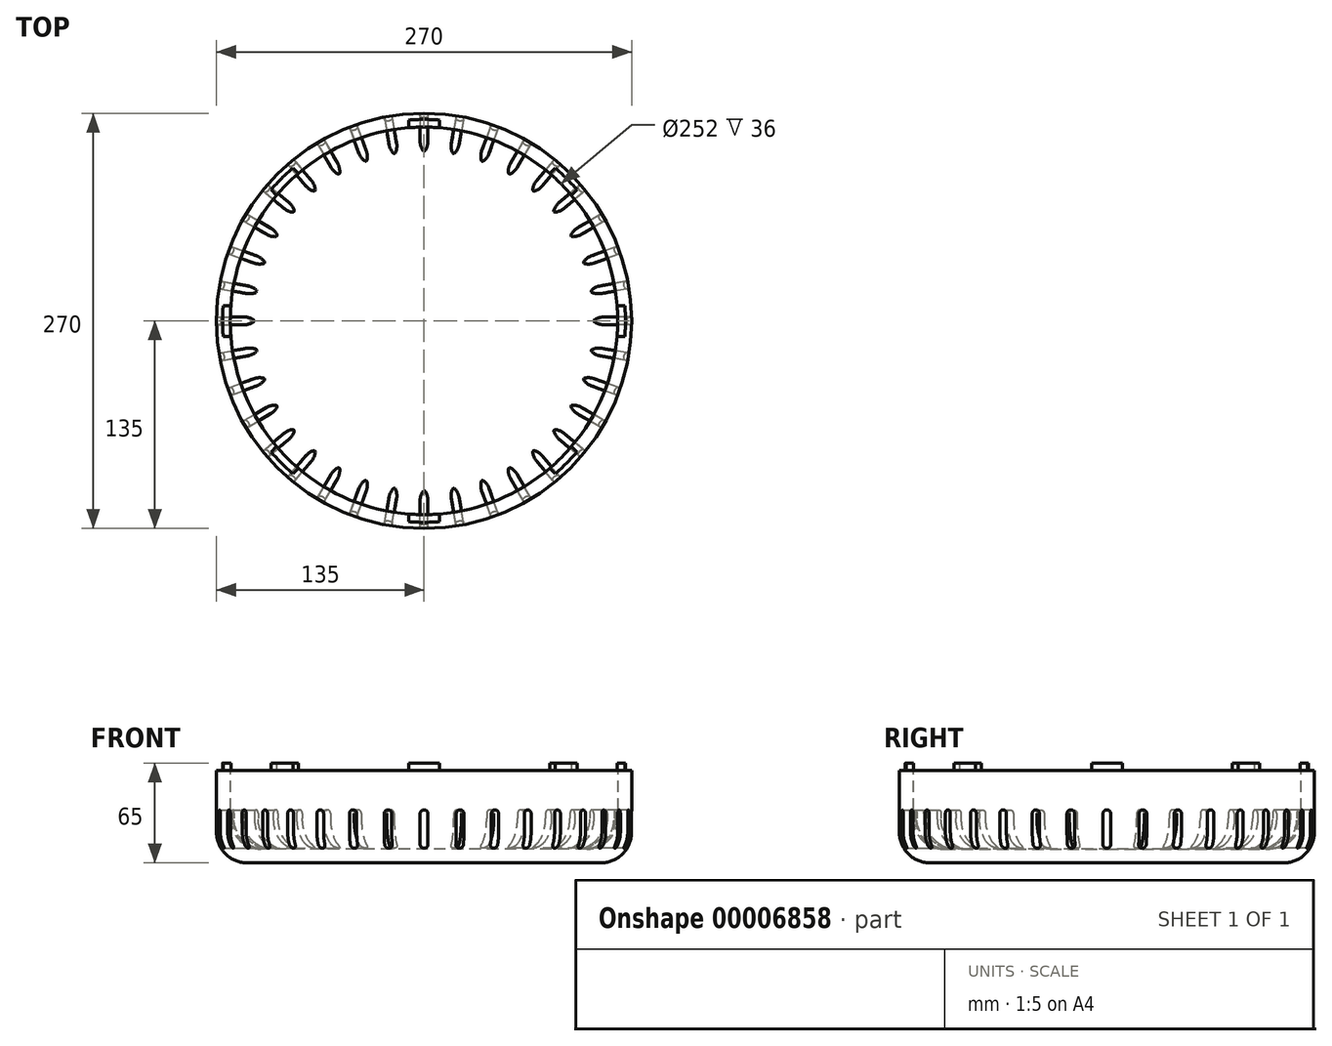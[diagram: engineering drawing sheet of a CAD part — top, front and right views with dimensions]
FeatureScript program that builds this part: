
annotation { "Feature Type Name" : "Feature", "Feature Type Description" : "" }
export const myFeature = defineFeature(function(context is Context, id is Id, definition is map)
    precondition{}
    {
        {
            var Q0;
            Q0=qCreatedBy(makeId("Top.planeOp"),FACE);
            var sketch = newSketch(context, id + "F0", { "sketchPlane" : qUnion([Q0])});
            skCircle(sketch, "E0", {"center": v(0, 0) * mm, "radius": 126 * mm});
            skCircle(sketch, "E1", {"center": v(0, 0) * mm, "radius": 135 * mm});
            skSolve(sketch);
        }
        {
            var Q0;
            Q0=qSketchRegion(id+"F0",true);
            var Q1;
            Q1=makeQuery(id+"F0.imprint","IMPRINT",FACE,{"disambiguationData":[TD([[makeQuery(id+"F0.imprint","IMPRINT",EDGE,{"derivedFrom":sQuery(id+"F0.wireOp",EDGE,"ITGFbY2j-F6Gs-mvNy-kfQ0-MyUqCA95ELIB")}),-1.0]])]});
            var Q2;
            Q2=makeQuery(id+"F0.imprint","IMPRINT",FACE,{"disambiguationData":[TD([[makeQuery(id+"F0.imprint","IMPRINT",EDGE,{"derivedFrom":sQuery(id+"F0.wireOp",EDGE,"ITGFbY2j-F6Gs-mvNy-kfQ0-MyUqCA95ELIB")}),1.0]])]});
            var Q3;
            Q3=makeQuery(id+"F0.imprint","IMPRINT",FACE,{"disambiguationData":[TD([[makeQuery(id+"F0.imprint","IMPRINT",EDGE,{"derivedFrom":sQuery(id+"F0.wireOp",EDGE,"E0")}),1.0]])]});
            extrude(context, id + "F1", {"entities" : qUnion([Q0, Q1, Q2, Q3]), "oppositeDirection" : true, "depth" : 30 * mm});
        }
        {
            var Q0;
            Q0=makeQuery(id+"F0.imprint","IMPRINT",FACE,{"disambiguationData":[TD([[makeQuery(id+"F0.imprint","IMPRINT",EDGE,{"derivedFrom":sQuery(id+"F0.wireOp",EDGE,"E0")}),-1.0]])]});
            extrude(context, id + "F2", {"entities" : qUnion([Q0]), "operationType" : NewBodyOperationType.ADD, "depth" : 30 * mm});
        }
        {
            var Q0;
            Q0=makeQuery(id+"F1.opExtrude","CAP_FACE",FACE,{"disambiguationData":[OSD([sQuery(id+"F0.wireOp",EDGE,"E1")])],"isStart":true});
            shell(context, id + "F3", {"entities" : qUnion([Q0]), "thickness" : 9 * mm});
        }
        {
            var Q0;
            Q0=makeQuery(id+"F2.opExtrude","CAP_FACE",FACE,{"disambiguationData":[OSD([sQuery(id+"F0.wireOp",EDGE,"E0"),sQuery(id+"F0.wireOp",EDGE,"E1")])],"isStart":false});
            var sketch = newSketch(context, id + "F4", { "sketchPlane" : qUnion([Q0])});
            skCircle(sketch, "E2", {"center": v(0, 0) * mm, "radius": 126 * mm});
            skCircle(sketch, "E3", {"center": v(0, 0) * mm, "radius": 131 * mm});
            skLineSegment(sketch, "E4", {"start": v(-130.62, -10) * mm, "end": v(-125.6, -10) * mm});
            skLineSegment(sketch, "E5", {"start": v(-130.62, 10) * mm, "end": v(-125.6, 10) * mm});
            skLineSegment(sketch, "E6", {"start": v(125.6, 10) * mm, "end": v(130.62, 10) * mm});
            skLineSegment(sketch, "E7", {"start": v(125.6, -10) * mm, "end": v(130.62, -10) * mm});
            skLineSegment(sketch, "E8", {"start": v(-10, 125.6) * mm, "end": v(-10, 130.62) * mm});
            skLineSegment(sketch, "E9", {"start": v(10, 125.6) * mm, "end": v(10, 130.62) * mm});
            skPoint(sketch, "E10", {"position": v(0, 126) * mm});
            skPoint(sketch, "E11", {"position": v(-126, 0) * mm});
            skPoint(sketch, "E12", {"position": v(126, 0) * mm});
            skPoint(sketch, "E13", {"position": v(0, -126) * mm});
            skLineSegment(sketch, "E14", {"start": v(-128.11, 10) * mm, "end": v(-128.11, -10) * mm});
            skPoint(sketch, "E15", {"position": v(-128.11, 0) * mm});
            skLineSegment(sketch, "E16", {"start": v(164.04, 10) * mm, "end": v(164.04, -10) * mm});
            skPoint(sketch, "E17", {"position": v(164.04, 0) * mm});
            skLineSegment(sketch, "E18", {"start": v(-10, -125.6) * mm, "end": v(-10, -130.62) * mm});
            skLineSegment(sketch, "E19", {"start": v(10, -125.6) * mm, "end": v(10, -130.62) * mm});
            skLineSegment(sketch, "E20", {"start": v(-10, -126.16) * mm, "end": v(10, -126.16) * mm});
            skPoint(sketch, "E21", {"position": v(0, -126.16) * mm});
            skLineSegment(sketch, "E22", {"start": v(-10, 175.22) * mm, "end": v(10, 175.22) * mm});
            skPoint(sketch, "E23", {"position": v(0, 175.22) * mm});
            skLineSegment(sketch, "E24", {"start": v(0, 0) * mm, "end": v(0, 71.25) * mm});
            skLineSegment(sketch, "E25", {"start": v(23.85, 0) * mm, "end": v(0, 0) * mm});
            skLineSegment(sketch, "E26", {"start": v(-90.59, 90.59) * mm, "end": v(90.59, -90.59) * mm});
            skLineSegment(sketch, "E27", {"start": v(-43.26, -43.26) * mm, "end": v(90.59, 90.59) * mm});
            skLineSegment(sketch, "E28", {"start": v(81.74, 95.89) * mm, "end": v(85.29, 99.43) * mm});
            skLineSegment(sketch, "E29", {"start": v(95.89, 81.74) * mm, "end": v(99.43, 85.29) * mm});
            skLineSegment(sketch, "E30", {"start": v(83.52, 97.66) * mm, "end": v(97.66, 83.52) * mm});
            skPoint(sketch, "E31", {"position": v(90.59, 90.59) * mm});
            skLineSegment(sketch, "E32", {"start": v(-99.43, -85.29) * mm, "end": v(-95.89, -81.74) * mm});
            skLineSegment(sketch, "E33", {"start": v(-85.29, -99.43) * mm, "end": v(-81.74, -95.89) * mm});
            skLineSegment(sketch, "E34", {"start": v(-50.33, -36.19) * mm, "end": v(-36.19, -50.33) * mm});
            skPoint(sketch, "E35", {"position": v(-43.26, -43.26) * mm});
            skLineSegment(sketch, "E36", {"start": v(95.89, -81.74) * mm, "end": v(99.43, -85.29) * mm});
            skLineSegment(sketch, "E37", {"start": v(81.74, -95.89) * mm, "end": v(85.29, -99.43) * mm});
            skLineSegment(sketch, "E38", {"start": v(83.52, -97.66) * mm, "end": v(97.66, -83.52) * mm});
            skPoint(sketch, "E39", {"position": v(90.59, -90.59) * mm});
            skLineSegment(sketch, "E40", {"start": v(-85.29, 99.43) * mm, "end": v(-81.74, 95.89) * mm});
            skLineSegment(sketch, "E41", {"start": v(-99.43, 85.29) * mm, "end": v(-95.89, 81.74) * mm});
            skLineSegment(sketch, "E42", {"start": v(-97.66, 83.52) * mm, "end": v(-83.52, 97.66) * mm});
            skPoint(sketch, "E43", {"position": v(-90.59, 90.59) * mm});
            skSolve(sketch);
        }
        {
            var Q0;
            {var subQ5=sQuery(id+"F4.wireOp",EDGE,"E14");Q0=makeQuery(id+"F4.imprint","IMPRINT",FACE,{"disambiguationData":[TD([[makeQuery(id+"F4.imprint","IMPRINT",EDGE,{"derivedFrom":subQ5}),-1.0]])]});}
            var Q1;
            {var subQ5=sQuery(id+"F4.wireOp",EDGE,"E14");Q1=makeQuery(id+"F4.imprint","IMPRINT",FACE,{"disambiguationData":[TD([[makeQuery(id+"F4.imprint","IMPRINT",EDGE,{"derivedFrom":subQ5}),1.0]])]});}
            var Q2;
            {var subQ5=sQuery(id+"F4.wireOp",EDGE,"E22");Q2=makeQuery(id+"F4.imprint","IMPRINT",FACE,{"disambiguationData":[TD([[makeQuery(id+"F4.imprint","IMPRINT",EDGE,{"derivedFrom":subQ5}),-1.0]])]});}
            var Q3;
            {var subQ5=sQuery(id+"F4.wireOp",EDGE,"E22");Q3=makeQuery(id+"F4.imprint","IMPRINT",FACE,{"disambiguationData":[TD([[makeQuery(id+"F4.imprint","IMPRINT",EDGE,{"derivedFrom":subQ5}),1.0]])]});}
            var Q4;
            {var subQ5=sQuery(id+"F4.wireOp",EDGE,"E16");Q4=makeQuery(id+"F4.imprint","IMPRINT",FACE,{"disambiguationData":[TD([[makeQuery(id+"F4.imprint","IMPRINT",EDGE,{"derivedFrom":subQ5}),1.0]])]});}
            var Q5;
            {var subQ5=sQuery(id+"F4.wireOp",EDGE,"E20");Q5=makeQuery(id+"F4.imprint","IMPRINT",FACE,{"disambiguationData":[TD([[makeQuery(id+"F4.imprint","IMPRINT",EDGE,{"derivedFrom":subQ5}),-1.0]])]});}
            var Q6;
            {var subQ5=sQuery(id+"F4.wireOp",EDGE,"E20");Q6=makeQuery(id+"F4.imprint","IMPRINT",FACE,{"disambiguationData":[TD([[makeQuery(id+"F4.imprint","IMPRINT",EDGE,{"derivedFrom":subQ5}),1.0]])]});}
            var Q7;
            {var subQ5=sQuery(id+"F4.wireOp",EDGE,"E16");Q7=makeQuery(id+"F4.imprint","IMPRINT",FACE,{"disambiguationData":[TD([[makeQuery(id+"F4.imprint","IMPRINT",EDGE,{"derivedFrom":subQ5}),-1.0]])]});}
            var Q8;
            {var subQ0=sQuery(id+"F4.wireOp",EDGE,"E6");Q8=makeQuery(id+"F4.imprint","IMPRINT",FACE,{"disambiguationData":[TD([[makeQuery(id+"F4.imprint","IMPRINT",EDGE,{"derivedFrom":subQ0}),-1.0]])]});}
            var Q9;
            {var subQ0=sQuery(id+"F4.wireOp",EDGE,"E8");Q9=makeQuery(id+"F4.imprint","IMPRINT",FACE,{"disambiguationData":[TD([[makeQuery(id+"F4.imprint","IMPRINT",EDGE,{"derivedFrom":subQ0}),-1.0]])]});}
            extrude(context, id + "F5", {"entities" : qUnion([Q0, Q1, Q2, Q3, Q4, Q5, Q6, Q7, Q8, Q9]), "operationType" : NewBodyOperationType.ADD, "depth" : 5 * mm});
        }
        {
            var Q0;
            {var subQ4=sQuery(id+"F4.wireOp",EDGE,"E3");var subQ6=sQuery(id+"F4.wireOp",EDGE,"E40");var subQ7=makeQuery(id+"F4.imprint","INTERSECT",VERTEX,{"derivedFrom":[subQ4,subQ6]});Q0=makeQuery(id+"F4.imprint","IMPRINT",FACE,{"disambiguationData":[TD([[makeQuery(id+"F4.imprint","IMPRINT",EDGE,{"disambiguationData":[TD([[subQ7,-1.0]])],"derivedFrom":subQ4}),1.0]])]});}
            var Q1;
            {var subQ0=sQuery(id+"F4.wireOp",EDGE,"E41");var subQ1=sQuery(id+"F4.wireOp",EDGE,"E2");var subQ2=makeQuery(id+"F4.imprint","INTERSECT",VERTEX,{"derivedFrom":[subQ1,subQ0]});Q1=makeQuery(id+"F4.imprint","IMPRINT",FACE,{"disambiguationData":[TD([[makeQuery(id+"F4.imprint","IMPRINT",EDGE,{"disambiguationData":[TD([[subQ2,1.0]])],"derivedFrom":subQ1}),-1.0]])]});}
            var Q2;
            {var subQ0=sQuery(id+"F4.wireOp",EDGE,"E40");var subQ1=sQuery(id+"F4.wireOp",EDGE,"E2");var subQ2=makeQuery(id+"F4.imprint","INTERSECT",VERTEX,{"derivedFrom":[subQ1,subQ0]});Q2=makeQuery(id+"F4.imprint","IMPRINT",FACE,{"disambiguationData":[TD([[makeQuery(id+"F4.imprint","IMPRINT",EDGE,{"disambiguationData":[TD([[subQ2,-1.0]])],"derivedFrom":subQ1}),-1.0]])]});}
            var Q3;
            {var subQ2=sQuery(id+"F4.wireOp",EDGE,"E28");var subQ5=sQuery(id+"F4.wireOp",EDGE,"E3");var subQ8=makeQuery(id+"F4.imprint","INTERSECT",VERTEX,{"derivedFrom":[subQ5,subQ2]});Q3=makeQuery(id+"F4.imprint","IMPRINT",FACE,{"disambiguationData":[TD([[makeQuery(id+"F4.imprint","IMPRINT",EDGE,{"disambiguationData":[TD([[subQ8,1.0]])],"derivedFrom":subQ5}),1.0]])]});}
            var Q4;
            {var subQ0=sQuery(id+"F4.wireOp",EDGE,"E28");var subQ1=sQuery(id+"F4.wireOp",EDGE,"E2");var subQ2=makeQuery(id+"F4.imprint","INTERSECT",VERTEX,{"derivedFrom":[subQ1,subQ0]});Q4=makeQuery(id+"F4.imprint","IMPRINT",FACE,{"disambiguationData":[TD([[makeQuery(id+"F4.imprint","IMPRINT",EDGE,{"disambiguationData":[TD([[subQ2,1.0]])],"derivedFrom":subQ1}),-1.0]])]});}
            var Q5;
            {var subQ0=sQuery(id+"F4.wireOp",EDGE,"E29");var subQ1=sQuery(id+"F4.wireOp",EDGE,"E2");var subQ2=makeQuery(id+"F4.imprint","INTERSECT",VERTEX,{"derivedFrom":[subQ1,subQ0]});Q5=makeQuery(id+"F4.imprint","IMPRINT",FACE,{"disambiguationData":[TD([[makeQuery(id+"F4.imprint","IMPRINT",EDGE,{"disambiguationData":[TD([[subQ2,-1.0]])],"derivedFrom":subQ1}),-1.0]])]});}
            var Q6;
            {var subQ0=sQuery(id+"F4.wireOp",EDGE,"E36");var subQ1=sQuery(id+"F4.wireOp",EDGE,"E2");var subQ2=makeQuery(id+"F4.imprint","INTERSECT",VERTEX,{"derivedFrom":[subQ1,subQ0]});Q6=makeQuery(id+"F4.imprint","IMPRINT",FACE,{"disambiguationData":[TD([[makeQuery(id+"F4.imprint","IMPRINT",EDGE,{"disambiguationData":[TD([[subQ2,1.0]])],"derivedFrom":subQ1}),-1.0]])]});}
            var Q7;
            {var subQ0=sQuery(id+"F4.wireOp",EDGE,"E37");var subQ1=sQuery(id+"F4.wireOp",EDGE,"E2");var subQ2=makeQuery(id+"F4.imprint","INTERSECT",VERTEX,{"derivedFrom":[subQ1,subQ0]});Q7=makeQuery(id+"F4.imprint","IMPRINT",FACE,{"disambiguationData":[TD([[makeQuery(id+"F4.imprint","IMPRINT",EDGE,{"disambiguationData":[TD([[subQ2,-1.0]])],"derivedFrom":subQ1}),-1.0]])]});}
            var Q8;
            {var subQ1=sQuery(id+"F4.wireOp",EDGE,"E3");var subQ6=sQuery(id+"F4.wireOp",EDGE,"E36");var subQ7=makeQuery(id+"F4.imprint","INTERSECT",VERTEX,{"derivedFrom":[subQ1,subQ6]});Q8=makeQuery(id+"F4.imprint","IMPRINT",FACE,{"disambiguationData":[TD([[makeQuery(id+"F4.imprint","IMPRINT",EDGE,{"disambiguationData":[TD([[subQ7,1.0]])],"derivedFrom":subQ1}),1.0]])]});}
            var Q9;
            {var subQ0=sQuery(id+"F4.wireOp",EDGE,"E33");var subQ1=sQuery(id+"F4.wireOp",EDGE,"E2");var subQ2=makeQuery(id+"F4.imprint","INTERSECT",VERTEX,{"derivedFrom":[subQ1,subQ0]});Q9=makeQuery(id+"F4.imprint","IMPRINT",FACE,{"disambiguationData":[TD([[makeQuery(id+"F4.imprint","IMPRINT",EDGE,{"disambiguationData":[TD([[subQ2,1.0]])],"derivedFrom":subQ1}),-1.0]])]});}
            var Q10;
            {var subQ0=sQuery(id+"F4.wireOp",EDGE,"E32");var subQ1=sQuery(id+"F4.wireOp",EDGE,"E2");var subQ2=makeQuery(id+"F4.imprint","INTERSECT",VERTEX,{"derivedFrom":[subQ1,subQ0]});Q10=makeQuery(id+"F4.imprint","IMPRINT",FACE,{"disambiguationData":[TD([[makeQuery(id+"F4.imprint","IMPRINT",EDGE,{"disambiguationData":[TD([[subQ2,-1.0]])],"derivedFrom":subQ1}),-1.0]])]});}
            var Q11;
            {var subQ1=sQuery(id+"F4.wireOp",EDGE,"E3");var subQ5=sQuery(id+"F4.wireOp",EDGE,"E32");var subQ6=makeQuery(id+"F4.imprint","INTERSECT",VERTEX,{"derivedFrom":[subQ1,subQ5]});Q11=makeQuery(id+"F4.imprint","IMPRINT",FACE,{"disambiguationData":[TD([[makeQuery(id+"F4.imprint","IMPRINT",EDGE,{"disambiguationData":[TD([[subQ6,-1.0]])],"derivedFrom":subQ1}),1.0]])]});}
            extrude(context, id + "F6", {"entities" : qUnion([Q0, Q1, Q2, Q3, Q4, Q5, Q6, Q7, Q8, Q9, Q10, Q11]), "operationType" : NewBodyOperationType.ADD, "depth" : 5 * mm});
        }
        {
            var Q0;
            Q0=qCreatedBy(makeId("Front.planeOp"),FACE);
            cPlane(context, id + "F7", {"entities" : qUnion([Q0]), "cplaneType" : CPlaneType.OFFSET, "offset" : 120 * mm, "width" : 150 * mm, "height" : 150 * mm});
        }
        {
            var Q0;
            Q0=qCreatedBy(id+"F7.planeOp",FACE);
            var sketch = newSketch(context, id + "F8", { "sketchPlane" : qUnion([Q0])});
            skLineSegment(sketch, "E44.bottom", {"start": v(-2.5, -18) * mm, "end": v(2.5, -18) * mm});
            skLineSegment(sketch, "E44.top", {"start": v(-2.5, 2) * mm, "end": v(2.5, 2) * mm});
            skLineSegment(sketch, "E44.left", {"start": v(-2.5, -18) * mm, "end": v(-2.5, 2) * mm});
            skLineSegment(sketch, "E44.right", {"start": v(2.5, -18) * mm, "end": v(2.5, 2) * mm});
            skPoint(sketch, "E45", {"position": v(0, 2) * mm});
            skPoint(sketch, "E45.positionSnap0", {"position": v(0, 2) * mm});
            skPoint(sketch, "E46", {"position": v(0, 0) * mm});
            skArc(sketch, "E47", {"start": v(2.5, 2) * mm, "mid": v(0, 4.5) * mm, "end": v(-2.5, 2) * mm});
            skArc(sketch, "E48", {"start": v(-2.5, -18) * mm, "mid": v(0, -20.5) * mm, "end": v(2.5, -18) * mm});
            skSolve(sketch);
        }
        {
            var Q0;
            Q0=qSketchRegion(id+"F8",true);
            extrude(context, id + "F9", {"entities" : qUnion([Q0]), "depth" : 25 * mm});
        }
        {
            var Q0;
            Q0=makeQuery(id+"F9.opExtrude","SWEPT_BODY",BODY,{"disambiguationData":[OSD([sQuery(id+"F8.wireOp",EDGE,"E44.bottom"),sQuery(id+"F8.wireOp",EDGE,"E44.top"),sQuery(id+"F8.wireOp",EDGE,"E44.left"),sQuery(id+"F8.wireOp",EDGE,"E44.right")])]});
            var Q1;
            Q1=makeQuery(id+"F2.opExtrude","CAP_EDGE",EDGE,{"disambiguationData":[OSD([sQuery(id+"F0.wireOp",EDGE,"E1")])],"isStart":false});
            circularPattern(context, id + "F10", {"entities" : qUnion([Q0]), "axis" : qUnion([Q1]), "angle" : 10 * degree, "instanceCount" : 40});
        }
        {
            var Q0;
            Q0=makeQuery(id+"F9.opExtrude","SWEPT_BODY",BODY,{"disambiguationData":[OSD([sQuery(id+"F8.wireOp",EDGE,"E44.bottom"),sQuery(id+"F8.wireOp",EDGE,"E44.top"),sQuery(id+"F8.wireOp",EDGE,"E44.left"),sQuery(id+"F8.wireOp",EDGE,"E44.right")])]});
            var Q1;
            Q1=makeQuery(id+"F10.opPattern","COPY",BODY,{"derivedFrom":makeQuery(id+"F9.opExtrude","SWEPT_BODY",BODY,{"disambiguationData":[OSD([sQuery(id+"F8.wireOp",EDGE,"E44.bottom"),sQuery(id+"F8.wireOp",EDGE,"E44.top"),sQuery(id+"F8.wireOp",EDGE,"E44.left"),sQuery(id+"F8.wireOp",EDGE,"E44.right")])]}),"instanceName":"1"});
            var Q2;
            Q2=makeQuery(id+"F10.opPattern","COPY",BODY,{"derivedFrom":makeQuery(id+"F9.opExtrude","SWEPT_BODY",BODY,{"disambiguationData":[OSD([sQuery(id+"F8.wireOp",EDGE,"E44.bottom"),sQuery(id+"F8.wireOp",EDGE,"E44.top"),sQuery(id+"F8.wireOp",EDGE,"E44.left"),sQuery(id+"F8.wireOp",EDGE,"E44.right")])]}),"instanceName":"2"});
            var Q3;
            Q3=makeQuery(id+"F10.opPattern","COPY",BODY,{"derivedFrom":makeQuery(id+"F9.opExtrude","SWEPT_BODY",BODY,{"disambiguationData":[OSD([sQuery(id+"F8.wireOp",EDGE,"E44.bottom"),sQuery(id+"F8.wireOp",EDGE,"E44.top"),sQuery(id+"F8.wireOp",EDGE,"E44.left"),sQuery(id+"F8.wireOp",EDGE,"E44.right")])]}),"instanceName":"3"});
            var Q4;
            Q4=makeQuery(id+"F10.opPattern","COPY",BODY,{"derivedFrom":makeQuery(id+"F9.opExtrude","SWEPT_BODY",BODY,{"disambiguationData":[OSD([sQuery(id+"F8.wireOp",EDGE,"E44.bottom"),sQuery(id+"F8.wireOp",EDGE,"E44.top"),sQuery(id+"F8.wireOp",EDGE,"E44.left"),sQuery(id+"F8.wireOp",EDGE,"E44.right")])]}),"instanceName":"4"});
            var Q5;
            Q5=makeQuery(id+"F10.opPattern","COPY",BODY,{"derivedFrom":makeQuery(id+"F9.opExtrude","SWEPT_BODY",BODY,{"disambiguationData":[OSD([sQuery(id+"F8.wireOp",EDGE,"E44.bottom"),sQuery(id+"F8.wireOp",EDGE,"E44.top"),sQuery(id+"F8.wireOp",EDGE,"E44.left"),sQuery(id+"F8.wireOp",EDGE,"E44.right")])]}),"instanceName":"5"});
            var Q6;
            Q6=makeQuery(id+"F10.opPattern","COPY",BODY,{"derivedFrom":makeQuery(id+"F9.opExtrude","SWEPT_BODY",BODY,{"disambiguationData":[OSD([sQuery(id+"F8.wireOp",EDGE,"E44.bottom"),sQuery(id+"F8.wireOp",EDGE,"E44.top"),sQuery(id+"F8.wireOp",EDGE,"E44.left"),sQuery(id+"F8.wireOp",EDGE,"E44.right")])]}),"instanceName":"6"});
            var Q7;
            Q7=makeQuery(id+"F10.opPattern","COPY",BODY,{"derivedFrom":makeQuery(id+"F9.opExtrude","SWEPT_BODY",BODY,{"disambiguationData":[OSD([sQuery(id+"F8.wireOp",EDGE,"E44.bottom"),sQuery(id+"F8.wireOp",EDGE,"E44.top"),sQuery(id+"F8.wireOp",EDGE,"E44.left"),sQuery(id+"F8.wireOp",EDGE,"E44.right")])]}),"instanceName":"7"});
            var Q8;
            Q8=makeQuery(id+"F10.opPattern","COPY",BODY,{"derivedFrom":makeQuery(id+"F9.opExtrude","SWEPT_BODY",BODY,{"disambiguationData":[OSD([sQuery(id+"F8.wireOp",EDGE,"E44.bottom"),sQuery(id+"F8.wireOp",EDGE,"E44.top"),sQuery(id+"F8.wireOp",EDGE,"E44.left"),sQuery(id+"F8.wireOp",EDGE,"E44.right")])]}),"instanceName":"8"});
            var Q9;
            Q9=makeQuery(id+"F10.opPattern","COPY",BODY,{"derivedFrom":makeQuery(id+"F9.opExtrude","SWEPT_BODY",BODY,{"disambiguationData":[OSD([sQuery(id+"F8.wireOp",EDGE,"E44.bottom"),sQuery(id+"F8.wireOp",EDGE,"E44.top"),sQuery(id+"F8.wireOp",EDGE,"E44.left"),sQuery(id+"F8.wireOp",EDGE,"E44.right")])]}),"instanceName":"9"});
            var Q10;
            Q10=makeQuery(id+"F10.opPattern","COPY",BODY,{"derivedFrom":makeQuery(id+"F9.opExtrude","SWEPT_BODY",BODY,{"disambiguationData":[OSD([sQuery(id+"F8.wireOp",EDGE,"E44.bottom"),sQuery(id+"F8.wireOp",EDGE,"E44.top"),sQuery(id+"F8.wireOp",EDGE,"E44.left"),sQuery(id+"F8.wireOp",EDGE,"E44.right")])]}),"instanceName":"10"});
            var Q11;
            Q11=makeQuery(id+"F10.opPattern","COPY",BODY,{"derivedFrom":makeQuery(id+"F9.opExtrude","SWEPT_BODY",BODY,{"disambiguationData":[OSD([sQuery(id+"F8.wireOp",EDGE,"E44.bottom"),sQuery(id+"F8.wireOp",EDGE,"E44.top"),sQuery(id+"F8.wireOp",EDGE,"E44.left"),sQuery(id+"F8.wireOp",EDGE,"E44.right")])]}),"instanceName":"11"});
            var Q12;
            Q12=makeQuery(id+"F10.opPattern","COPY",BODY,{"derivedFrom":makeQuery(id+"F9.opExtrude","SWEPT_BODY",BODY,{"disambiguationData":[OSD([sQuery(id+"F8.wireOp",EDGE,"E44.bottom"),sQuery(id+"F8.wireOp",EDGE,"E44.top"),sQuery(id+"F8.wireOp",EDGE,"E44.left"),sQuery(id+"F8.wireOp",EDGE,"E44.right")])]}),"instanceName":"12"});
            var Q13;
            Q13=makeQuery(id+"F10.opPattern","COPY",BODY,{"derivedFrom":makeQuery(id+"F9.opExtrude","SWEPT_BODY",BODY,{"disambiguationData":[OSD([sQuery(id+"F8.wireOp",EDGE,"E44.bottom"),sQuery(id+"F8.wireOp",EDGE,"E44.top"),sQuery(id+"F8.wireOp",EDGE,"E44.left"),sQuery(id+"F8.wireOp",EDGE,"E44.right")])]}),"instanceName":"13"});
            var Q14;
            Q14=makeQuery(id+"F10.opPattern","COPY",BODY,{"derivedFrom":makeQuery(id+"F9.opExtrude","SWEPT_BODY",BODY,{"disambiguationData":[OSD([sQuery(id+"F8.wireOp",EDGE,"E44.bottom"),sQuery(id+"F8.wireOp",EDGE,"E44.top"),sQuery(id+"F8.wireOp",EDGE,"E44.left"),sQuery(id+"F8.wireOp",EDGE,"E44.right")])]}),"instanceName":"14"});
            var Q15;
            Q15=makeQuery(id+"F10.opPattern","COPY",BODY,{"derivedFrom":makeQuery(id+"F9.opExtrude","SWEPT_BODY",BODY,{"disambiguationData":[OSD([sQuery(id+"F8.wireOp",EDGE,"E44.bottom"),sQuery(id+"F8.wireOp",EDGE,"E44.top"),sQuery(id+"F8.wireOp",EDGE,"E44.left"),sQuery(id+"F8.wireOp",EDGE,"E44.right")])]}),"instanceName":"15"});
            var Q16;
            Q16=makeQuery(id+"F10.opPattern","COPY",BODY,{"derivedFrom":makeQuery(id+"F9.opExtrude","SWEPT_BODY",BODY,{"disambiguationData":[OSD([sQuery(id+"F8.wireOp",EDGE,"E44.bottom"),sQuery(id+"F8.wireOp",EDGE,"E44.top"),sQuery(id+"F8.wireOp",EDGE,"E44.left"),sQuery(id+"F8.wireOp",EDGE,"E44.right")])]}),"instanceName":"16"});
            var Q17;
            Q17=makeQuery(id+"F10.opPattern","COPY",BODY,{"derivedFrom":makeQuery(id+"F9.opExtrude","SWEPT_BODY",BODY,{"disambiguationData":[OSD([sQuery(id+"F8.wireOp",EDGE,"E44.bottom"),sQuery(id+"F8.wireOp",EDGE,"E44.top"),sQuery(id+"F8.wireOp",EDGE,"E44.left"),sQuery(id+"F8.wireOp",EDGE,"E44.right")])]}),"instanceName":"17"});
            var Q18;
            Q18=makeQuery(id+"F10.opPattern","COPY",BODY,{"derivedFrom":makeQuery(id+"F9.opExtrude","SWEPT_BODY",BODY,{"disambiguationData":[OSD([sQuery(id+"F8.wireOp",EDGE,"E44.bottom"),sQuery(id+"F8.wireOp",EDGE,"E44.top"),sQuery(id+"F8.wireOp",EDGE,"E44.left"),sQuery(id+"F8.wireOp",EDGE,"E44.right")])]}),"instanceName":"18"});
            var Q19;
            Q19=makeQuery(id+"F10.opPattern","COPY",BODY,{"derivedFrom":makeQuery(id+"F9.opExtrude","SWEPT_BODY",BODY,{"disambiguationData":[OSD([sQuery(id+"F8.wireOp",EDGE,"E44.bottom"),sQuery(id+"F8.wireOp",EDGE,"E44.top"),sQuery(id+"F8.wireOp",EDGE,"E44.left"),sQuery(id+"F8.wireOp",EDGE,"E44.right")])]}),"instanceName":"19"});
            var Q20;
            Q20=makeQuery(id+"F10.opPattern","COPY",BODY,{"derivedFrom":makeQuery(id+"F9.opExtrude","SWEPT_BODY",BODY,{"disambiguationData":[OSD([sQuery(id+"F8.wireOp",EDGE,"E44.bottom"),sQuery(id+"F8.wireOp",EDGE,"E44.top"),sQuery(id+"F8.wireOp",EDGE,"E44.left"),sQuery(id+"F8.wireOp",EDGE,"E44.right")])]}),"instanceName":"20"});
            var Q21;
            Q21=makeQuery(id+"F10.opPattern","COPY",BODY,{"derivedFrom":makeQuery(id+"F9.opExtrude","SWEPT_BODY",BODY,{"disambiguationData":[OSD([sQuery(id+"F8.wireOp",EDGE,"E44.bottom"),sQuery(id+"F8.wireOp",EDGE,"E44.top"),sQuery(id+"F8.wireOp",EDGE,"E44.left"),sQuery(id+"F8.wireOp",EDGE,"E44.right")])]}),"instanceName":"21"});
            var Q22;
            Q22=makeQuery(id+"F10.opPattern","COPY",BODY,{"derivedFrom":makeQuery(id+"F9.opExtrude","SWEPT_BODY",BODY,{"disambiguationData":[OSD([sQuery(id+"F8.wireOp",EDGE,"E44.bottom"),sQuery(id+"F8.wireOp",EDGE,"E44.top"),sQuery(id+"F8.wireOp",EDGE,"E44.left"),sQuery(id+"F8.wireOp",EDGE,"E44.right")])]}),"instanceName":"22"});
            var Q23;
            Q23=makeQuery(id+"F10.opPattern","COPY",BODY,{"derivedFrom":makeQuery(id+"F9.opExtrude","SWEPT_BODY",BODY,{"disambiguationData":[OSD([sQuery(id+"F8.wireOp",EDGE,"E44.bottom"),sQuery(id+"F8.wireOp",EDGE,"E44.top"),sQuery(id+"F8.wireOp",EDGE,"E44.left"),sQuery(id+"F8.wireOp",EDGE,"E44.right")])]}),"instanceName":"23"});
            var Q24;
            Q24=makeQuery(id+"F10.opPattern","COPY",BODY,{"derivedFrom":makeQuery(id+"F9.opExtrude","SWEPT_BODY",BODY,{"disambiguationData":[OSD([sQuery(id+"F8.wireOp",EDGE,"E44.bottom"),sQuery(id+"F8.wireOp",EDGE,"E44.top"),sQuery(id+"F8.wireOp",EDGE,"E44.left"),sQuery(id+"F8.wireOp",EDGE,"E44.right")])]}),"instanceName":"24"});
            var Q25;
            Q25=makeQuery(id+"F10.opPattern","COPY",BODY,{"derivedFrom":makeQuery(id+"F9.opExtrude","SWEPT_BODY",BODY,{"disambiguationData":[OSD([sQuery(id+"F8.wireOp",EDGE,"E44.bottom"),sQuery(id+"F8.wireOp",EDGE,"E44.top"),sQuery(id+"F8.wireOp",EDGE,"E44.left"),sQuery(id+"F8.wireOp",EDGE,"E44.right")])]}),"instanceName":"25"});
            var Q26;
            Q26=makeQuery(id+"F10.opPattern","COPY",BODY,{"derivedFrom":makeQuery(id+"F9.opExtrude","SWEPT_BODY",BODY,{"disambiguationData":[OSD([sQuery(id+"F8.wireOp",EDGE,"E44.bottom"),sQuery(id+"F8.wireOp",EDGE,"E44.top"),sQuery(id+"F8.wireOp",EDGE,"E44.left"),sQuery(id+"F8.wireOp",EDGE,"E44.right")])]}),"instanceName":"26"});
            var Q27;
            Q27=makeQuery(id+"F10.opPattern","COPY",BODY,{"derivedFrom":makeQuery(id+"F9.opExtrude","SWEPT_BODY",BODY,{"disambiguationData":[OSD([sQuery(id+"F8.wireOp",EDGE,"E44.bottom"),sQuery(id+"F8.wireOp",EDGE,"E44.top"),sQuery(id+"F8.wireOp",EDGE,"E44.left"),sQuery(id+"F8.wireOp",EDGE,"E44.right")])]}),"instanceName":"27"});
            var Q28;
            Q28=makeQuery(id+"F10.opPattern","COPY",BODY,{"derivedFrom":makeQuery(id+"F9.opExtrude","SWEPT_BODY",BODY,{"disambiguationData":[OSD([sQuery(id+"F8.wireOp",EDGE,"E44.bottom"),sQuery(id+"F8.wireOp",EDGE,"E44.top"),sQuery(id+"F8.wireOp",EDGE,"E44.left"),sQuery(id+"F8.wireOp",EDGE,"E44.right")])]}),"instanceName":"28"});
            var Q29;
            Q29=makeQuery(id+"F10.opPattern","COPY",BODY,{"derivedFrom":makeQuery(id+"F9.opExtrude","SWEPT_BODY",BODY,{"disambiguationData":[OSD([sQuery(id+"F8.wireOp",EDGE,"E44.bottom"),sQuery(id+"F8.wireOp",EDGE,"E44.top"),sQuery(id+"F8.wireOp",EDGE,"E44.left"),sQuery(id+"F8.wireOp",EDGE,"E44.right")])]}),"instanceName":"29"});
            var Q30;
            Q30=makeQuery(id+"F10.opPattern","COPY",BODY,{"derivedFrom":makeQuery(id+"F9.opExtrude","SWEPT_BODY",BODY,{"disambiguationData":[OSD([sQuery(id+"F8.wireOp",EDGE,"E44.bottom"),sQuery(id+"F8.wireOp",EDGE,"E44.top"),sQuery(id+"F8.wireOp",EDGE,"E44.left"),sQuery(id+"F8.wireOp",EDGE,"E44.right")])]}),"instanceName":"30"});
            var Q31;
            Q31=makeQuery(id+"F10.opPattern","COPY",BODY,{"derivedFrom":makeQuery(id+"F9.opExtrude","SWEPT_BODY",BODY,{"disambiguationData":[OSD([sQuery(id+"F8.wireOp",EDGE,"E44.bottom"),sQuery(id+"F8.wireOp",EDGE,"E44.top"),sQuery(id+"F8.wireOp",EDGE,"E44.left"),sQuery(id+"F8.wireOp",EDGE,"E44.right")])]}),"instanceName":"31"});
            var Q32;
            Q32=makeQuery(id+"F10.opPattern","COPY",BODY,{"derivedFrom":makeQuery(id+"F9.opExtrude","SWEPT_BODY",BODY,{"disambiguationData":[OSD([sQuery(id+"F8.wireOp",EDGE,"E44.bottom"),sQuery(id+"F8.wireOp",EDGE,"E44.top"),sQuery(id+"F8.wireOp",EDGE,"E44.left"),sQuery(id+"F8.wireOp",EDGE,"E44.right")])]}),"instanceName":"32"});
            var Q33;
            Q33=makeQuery(id+"F10.opPattern","COPY",BODY,{"derivedFrom":makeQuery(id+"F9.opExtrude","SWEPT_BODY",BODY,{"disambiguationData":[OSD([sQuery(id+"F8.wireOp",EDGE,"E44.bottom"),sQuery(id+"F8.wireOp",EDGE,"E44.top"),sQuery(id+"F8.wireOp",EDGE,"E44.left"),sQuery(id+"F8.wireOp",EDGE,"E44.right")])]}),"instanceName":"33"});
            var Q34;
            Q34=makeQuery(id+"F10.opPattern","COPY",BODY,{"derivedFrom":makeQuery(id+"F9.opExtrude","SWEPT_BODY",BODY,{"disambiguationData":[OSD([sQuery(id+"F8.wireOp",EDGE,"E44.bottom"),sQuery(id+"F8.wireOp",EDGE,"E44.top"),sQuery(id+"F8.wireOp",EDGE,"E44.left"),sQuery(id+"F8.wireOp",EDGE,"E44.right")])]}),"instanceName":"34"});
            var Q35;
            Q35=makeQuery(id+"F10.opPattern","COPY",BODY,{"derivedFrom":makeQuery(id+"F9.opExtrude","SWEPT_BODY",BODY,{"disambiguationData":[OSD([sQuery(id+"F8.wireOp",EDGE,"E44.bottom"),sQuery(id+"F8.wireOp",EDGE,"E44.top"),sQuery(id+"F8.wireOp",EDGE,"E44.left"),sQuery(id+"F8.wireOp",EDGE,"E44.right")])]}),"instanceName":"35"});
            var Q36;
            Q36=makeQuery(id+"F10.opPattern","COPY",BODY,{"derivedFrom":makeQuery(id+"F9.opExtrude","SWEPT_BODY",BODY,{"disambiguationData":[OSD([sQuery(id+"F8.wireOp",EDGE,"E44.bottom"),sQuery(id+"F8.wireOp",EDGE,"E44.top"),sQuery(id+"F8.wireOp",EDGE,"E44.left"),sQuery(id+"F8.wireOp",EDGE,"E44.right")])]}),"instanceName":"36"});
            var Q37;
            Q37=makeQuery(id+"F10.opPattern","COPY",BODY,{"derivedFrom":makeQuery(id+"F9.opExtrude","SWEPT_BODY",BODY,{"disambiguationData":[OSD([sQuery(id+"F8.wireOp",EDGE,"E44.bottom"),sQuery(id+"F8.wireOp",EDGE,"E44.top"),sQuery(id+"F8.wireOp",EDGE,"E44.left"),sQuery(id+"F8.wireOp",EDGE,"E44.right")])]}),"instanceName":"37"});
            var Q38;
            Q38=makeQuery(id+"F10.opPattern","COPY",BODY,{"derivedFrom":makeQuery(id+"F9.opExtrude","SWEPT_BODY",BODY,{"disambiguationData":[OSD([sQuery(id+"F8.wireOp",EDGE,"E44.bottom"),sQuery(id+"F8.wireOp",EDGE,"E44.top"),sQuery(id+"F8.wireOp",EDGE,"E44.left"),sQuery(id+"F8.wireOp",EDGE,"E44.right")])]}),"instanceName":"38"});
            var Q39;
            Q39=makeQuery(id+"F10.opPattern","COPY",BODY,{"derivedFrom":makeQuery(id+"F9.opExtrude","SWEPT_BODY",BODY,{"disambiguationData":[OSD([sQuery(id+"F8.wireOp",EDGE,"E44.bottom"),sQuery(id+"F8.wireOp",EDGE,"E44.top"),sQuery(id+"F8.wireOp",EDGE,"E44.left"),sQuery(id+"F8.wireOp",EDGE,"E44.right")])]}),"instanceName":"39"});
            var Q40;
            Q40=makeQuery(id+"F1.opExtrude","SWEPT_BODY",BODY,{"disambiguationData":[OSD([sQuery(id+"F0.wireOp",EDGE,"E1")])]});
            booleanBodies(context, id + "F11", {"operationType" : BooleanOperationType.SUBTRACTION, "tools" : qUnion([Q0, Q1, Q2, Q3, Q4, Q5, Q6, Q7, Q8, Q9, Q10, Q11, Q12, Q13, Q14, Q15, Q16, Q17, Q18, Q19, Q20, Q21, Q22, Q23, Q24, Q25, Q26, Q27, Q28, Q29, Q30, Q31, Q32, Q33, Q34, Q35, Q36, Q37, Q38, Q39]), "targets" : qUnion([Q40])});
        }
        {
            var Q0;
            Q0=makeQuery(id+"F1.opExtrude","CAP_EDGE",EDGE,{"disambiguationData":[OSD([sQuery(id+"F0.wireOp",EDGE,"E1")])],"isStart":false});
            var Q1;
            Q1=makeQuery(id+"F3.opShell","OFFSET_EDGE",EDGE,{"disambiguationData":[OSD([sQuery(id+"F0.wireOp",EDGE,"E1")])]});
            fillet(context, id + "F12", {"entities" : qUnion([Q0, Q1]), "radius" : 20 * mm, "tangentPropagation" : true, "allowEdgeOverflow" : false});
        }
    });
